# Revit family: Sink-Pedestal-KOHLER-Rêve-K-5152
name_source: partatom
category: Plumbing Fixtures
revit_build: Autodesk Revit 2015 (Build: 20140606_1530(x64)
units: mm (PartAtom-declared; Revit-internal decimal feet)

## types (2) — shared parameters
ADA Compliant = No
Assembly Code = D2010400
CW Connection = No
Cold Water Inlet = Cold Water Inlet
Date Modified = 04/03/2019
Default Elevation = 0"
Drain Included = No
Finish = Kohler-Fireclay-0-White
HW Connection = No
Height = 35 1/2"
Hot Water Inlet = Hot Water Inlet
Length = 23 5/8"
Manufacturer = KOHLER Co.
MasterFormat 1995 = 15410
MasterFormat 2004 = 22.41.16
Material = Fireclay
Product Documentation Link = https://www.us.kohler.com
Product Name = Rêve
Product Page URL = http://www.us.kohler.com
URL = https://www.us.kohler.com
Vent Connection = No
Waste Connection = Yes
Waste Water Outlet = Waste Water Outlet
WaterSense Certified = No
Width = 18 5/16"

## per-type parameters (varying)
| type | 8 inch Widespread Faucet hole | Description | Hole Distance | Model | Single Faucet hole | Type |
| Single Faucet hole, 0- White | No | 23 inch pedestal bathroom sink with single faucet hole | 26" | K-5152-1-0 | Yes | 1 |
| 8 inch Widespread Faucet hole, 0- White | Yes | 23 inch pedestal bathroom sink with 8 inch widespread faucet holes | 8" | K-5152-8-0 | No | 2 |

## geometry (parser evidence)
native form markers: Sweep x6
no freeform markers — native parametric forms only
